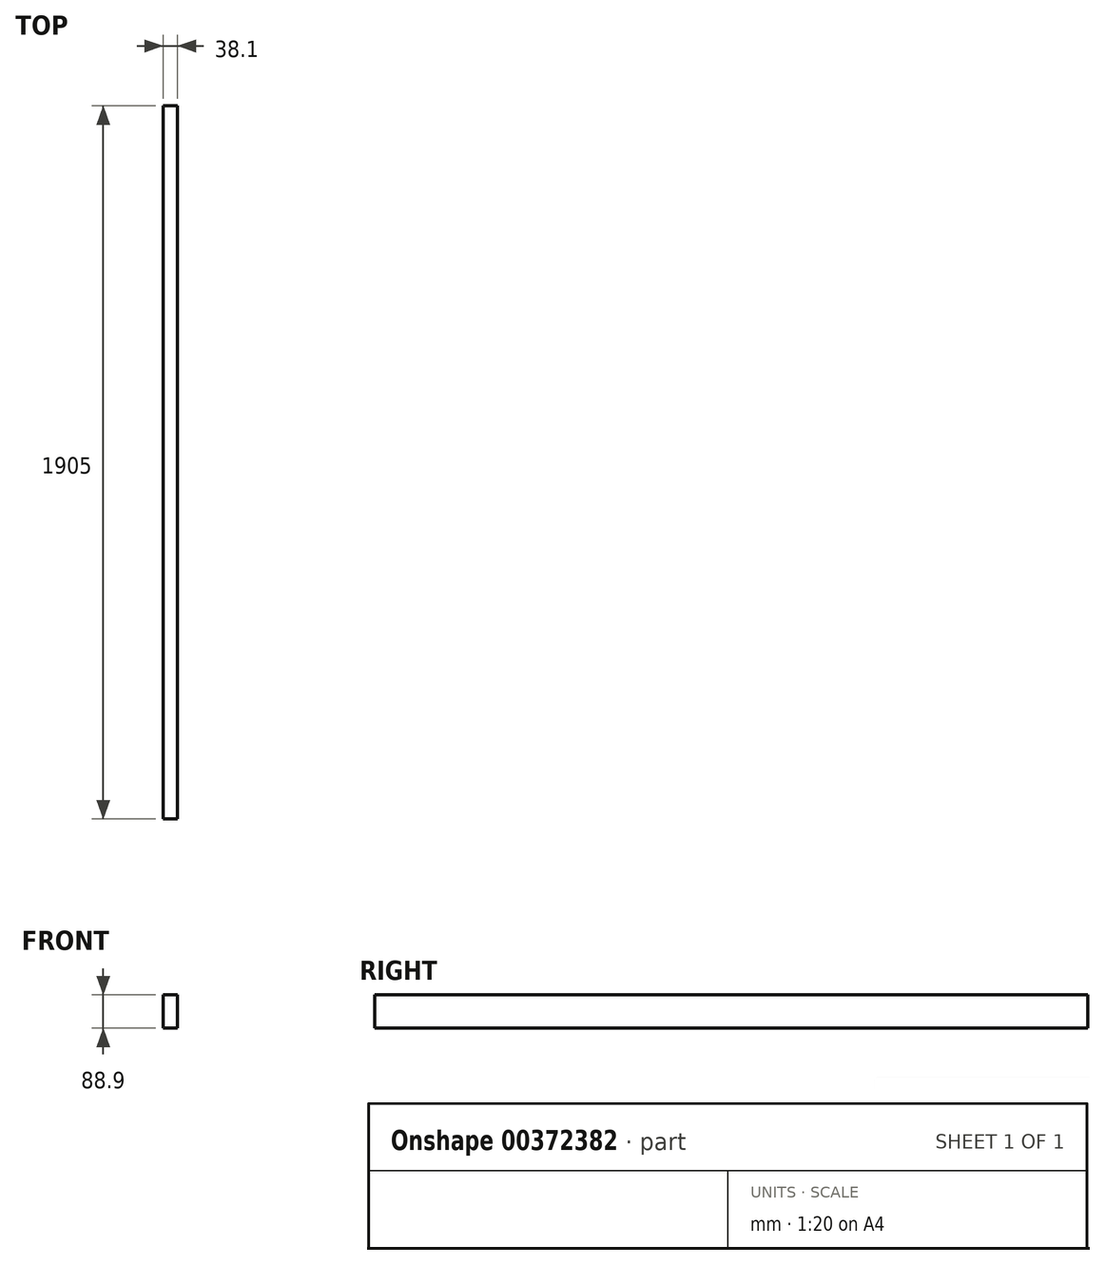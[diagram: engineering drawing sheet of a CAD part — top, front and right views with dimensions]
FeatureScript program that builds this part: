
annotation { "Feature Type Name" : "Feature", "Feature Type Description" : "" }
export const myFeature = defineFeature(function(context is Context, id is Id, definition is map)
    precondition{}
    {
        {
            var Q0;
            Q0=qCreatedBy(makeId("Front.planeOp"),FACE);
            var sketch = newSketch(context, id + "F0", { "sketchPlane" : qUnion([Q0])});
            skLineSegment(sketch, "E0.bottom", {"start": v(-19.05, 44.45) * mm, "end": v(19.05, 44.45) * mm});
            skLineSegment(sketch, "E0.top", {"start": v(-19.05, -44.45) * mm, "end": v(19.05, -44.45) * mm});
            skLineSegment(sketch, "E0.left", {"start": v(-19.05, 44.45) * mm, "end": v(-19.05, -44.45) * mm});
            skLineSegment(sketch, "E0.right", {"start": v(19.05, 44.45) * mm, "end": v(19.05, -44.45) * mm});
            skPoint(sketch, "E0.middle", {"position": v(0, 0) * mm});
            skSolve(sketch);
        }
        {
            var Q0;
            Q0=qSketchRegion(id+"F0",true);
            extrude(context, id + "F1", {"entities" : qUnion([Q0]), "endBound" : BoundingType.SYMMETRIC, "oppositeDirection" : true, "depth" : 1905 * mm});
        }
    });
